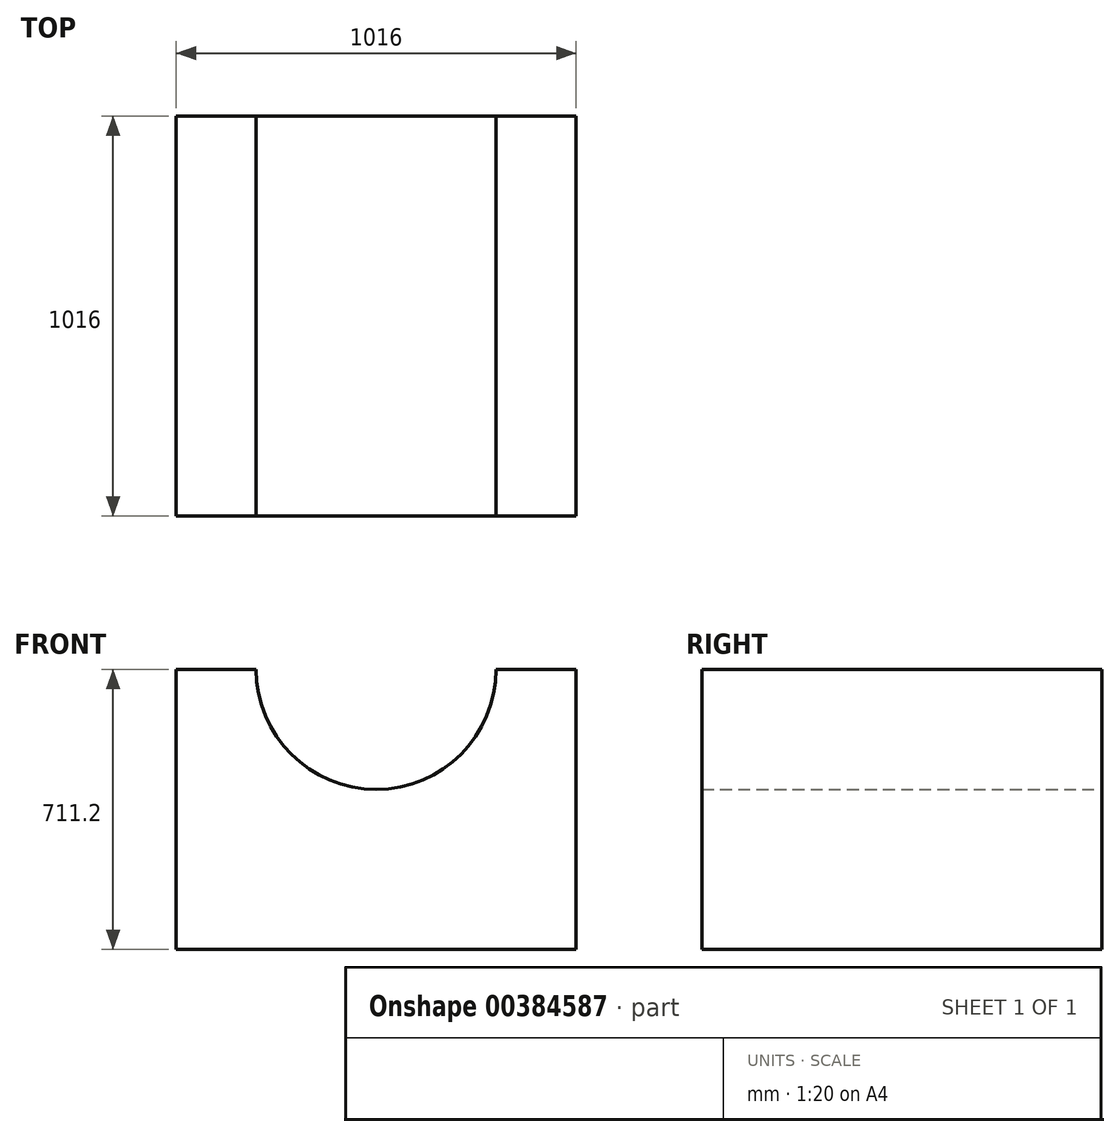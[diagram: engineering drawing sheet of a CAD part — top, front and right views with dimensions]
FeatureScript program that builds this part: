
annotation { "Feature Type Name" : "Feature", "Feature Type Description" : "" }
export const myFeature = defineFeature(function(context is Context, id is Id, definition is map)
    precondition{}
    {
        {
            var Q0;
            Q0=qCreatedBy(makeId("Front.planeOp"),FACE);
            var sketch = newSketch(context, id + "F0", { "sketchPlane" : qUnion([Q0])});
            skLineSegment(sketch, "E0", {"start": v(0, 0) * mm, "end": v(1016, 0) * mm});
            skLineSegment(sketch, "E1", {"start": v(1016, 0) * mm, "end": v(1016, 711.2) * mm});
            skLineSegment(sketch, "E2", {"start": v(0, 0) * mm, "end": v(0, 711.2) * mm});
            skLineSegment(sketch, "E3", {"start": v(0, 711.2) * mm, "end": v(203.2, 711.2) * mm});
            skLineSegment(sketch, "E4", {"start": v(1016, 711.2) * mm, "end": v(812.8, 711.2) * mm});
            skArc(sketch, "E5", {"start": v(203.2, 711.2) * mm, "mid": v(508, 406.4) * mm, "end": v(812.8, 711.2) * mm});
            skSolve(sketch);
        }
        {
            var Q0;
            Q0=makeQuery(id+"F0.imprint","IMPRINT",FACE,{"disambiguationData":[TD([[makeQuery(id+"F0.imprint","IMPRINT",EDGE,{"derivedFrom":sQuery(id+"F0.wireOp",EDGE,"E0")}),1.0]])]});
            extrude(context, id + "F1", {"entities" : qUnion([Q0]), "depth" : 1016 * mm});
        }
    });
